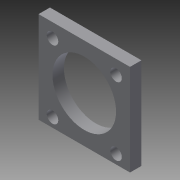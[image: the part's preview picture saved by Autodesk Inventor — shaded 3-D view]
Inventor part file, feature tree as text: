
AUTODESK INVENTOR PART (.ipt)
format: ipt  version: 2013 (Build 170138000, 138)  size: 91,648 bytes
history: native  units: in
note: dims shown in document units (in); Inventor stores cm internally (conversion verified against a paired STEP export)
features: extrude x1, sketch x1
ambient origin geometry x8: Origin, YZ Plane, XZ Plane, XY Plane, X Axis, Y Axis, Z Axis, Center Point
bodies: Solid1 (feature_tree)
feature tree (2):
  extrude  "Extrusion1"  Depth=2.0in
  sketch  "Sketch1"  dims[d0=2.0in d1=2.0in d2=1.39in d3=0.252in d4=0.252in d5=0.252in d6=0.252in d7=0.25in d8=0.0in]
